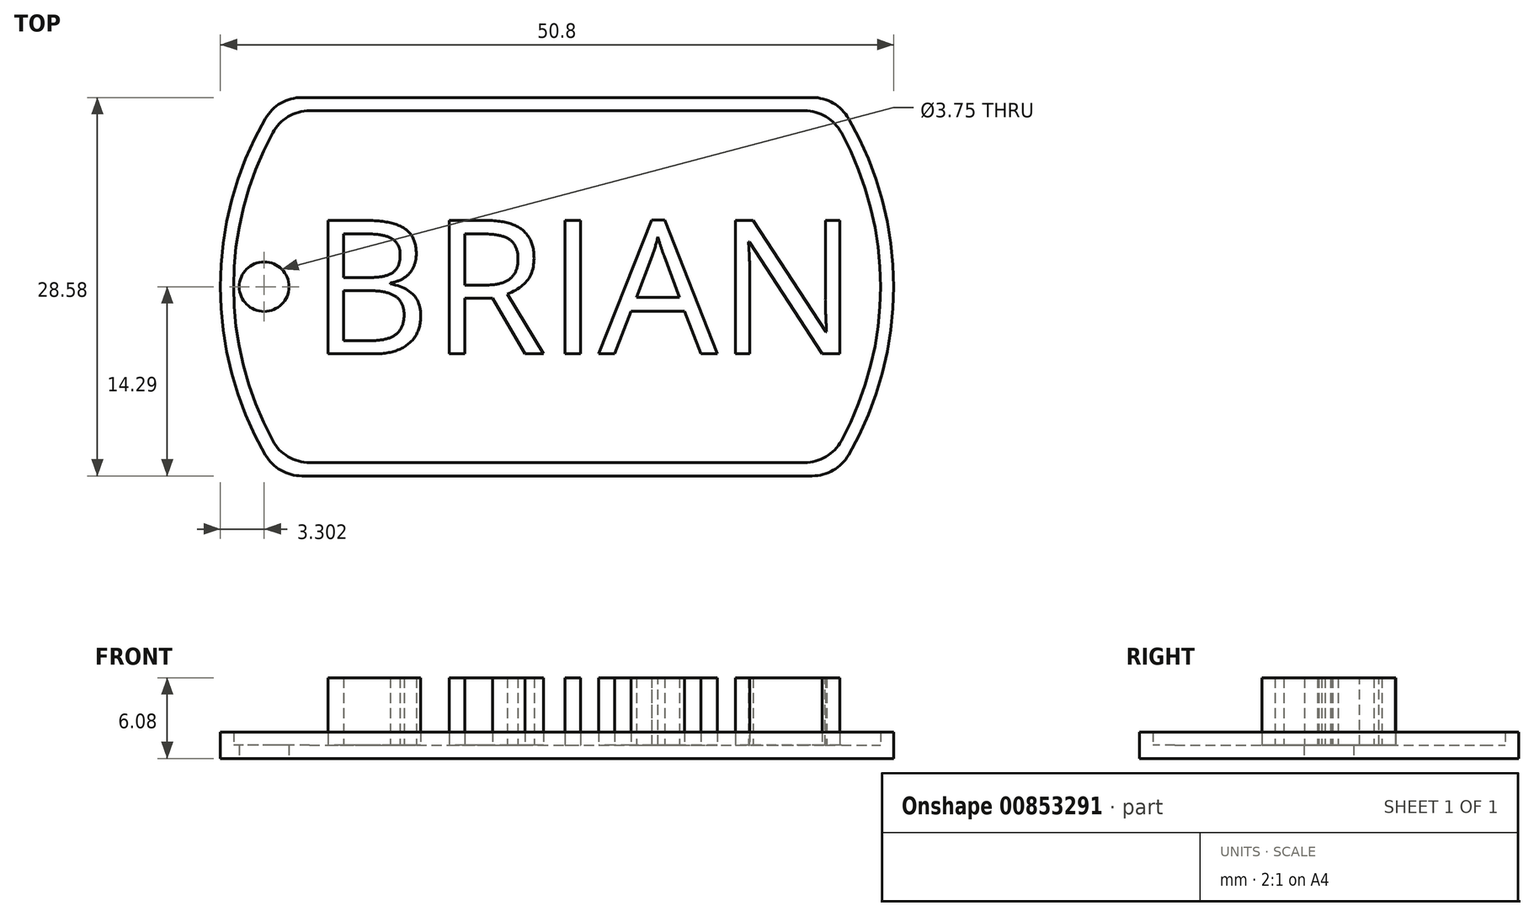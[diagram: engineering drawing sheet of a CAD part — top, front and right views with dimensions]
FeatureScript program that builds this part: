
annotation { "Feature Type Name" : "Feature", "Feature Type Description" : "" }
export const myFeature = defineFeature(function(context is Context, id is Id, definition is map)
    precondition{}
    {
        {
            var Q0;
            Q0=qCreatedBy(makeId("Top.planeOp"),FACE);
            var sketch = newSketch(context, id + "F0", { "sketchPlane" : qUnion([Q0])});
            skArc(sketch, "E0", {"start": v(-22, 12.7) * mm, "mid": v(-25.4, 0) * mm, "end": v(-22, -12.7) * mm});
            skLineSegment(sketch, "E1.top", {"start": v(-19.25, -14.29) * mm, "end": v(19.25, -14.29) * mm});
            skArc(sketch, "E2.trimOffspring", {"start": v(22, -12.7) * mm, "mid": v(25.4, 0) * mm, "end": v(22, 12.7) * mm});
            skLineSegment(sketch, "E3", {"start": v(-19.25, 14.29) * mm, "end": v(19.25, 14.29) * mm});
            skPoint(sketch, "E4.visualSharp", {"position": v(-21, 14.29) * mm});
            skArc(sketch, "E4.filletArc", {"start": v(-19.25, 14.29) * mm, "mid": v(-20.83, 13.86) * mm, "end": v(-22, 12.7) * mm});
            skPoint(sketch, "E5.visualSharp", {"position": v(21, 14.29) * mm});
            skArc(sketch, "E5.filletArc", {"start": v(22, 12.7) * mm, "mid": v(20.83, 13.86) * mm, "end": v(19.25, 14.29) * mm});
            skPoint(sketch, "E6.visualSharp", {"position": v(21, -14.29) * mm});
            skArc(sketch, "E6.filletArc", {"start": v(19.25, -14.29) * mm, "mid": v(20.83, -13.86) * mm, "end": v(22, -12.7) * mm});
            skPoint(sketch, "E7.visualSharp", {"position": v(-21, -14.29) * mm});
            skArc(sketch, "E7.filletArc", {"start": v(-22, -12.7) * mm, "mid": v(-20.83, -13.86) * mm, "end": v(-19.25, -14.29) * mm});
            skCircle(sketch, "E8", {"center": v(-22.1, 0) * mm, "radius": 1.87 * mm});
            skSolve(sketch);
        }
        {
            var Q0;
            Q0=makeQuery(id+"F0.imprint","IMPRINT",FACE,{"disambiguationData":[TD([[makeQuery(id+"F0.imprint","IMPRINT",EDGE,{"derivedFrom":sQuery(id+"F0.wireOp",EDGE,"E0")}),1.0]])]});
            extrude(context, id + "F1", {"entities" : qUnion([Q0]), "depth" : 1 * mm, "offsetDistance" : 25.4 * mm});
        }
        {
            var Q0;
            Q0=makeQuery(id+"F1.opExtrude","CAP_FACE",FACE,{"disambiguationData":[OSD([sQuery(id+"F0.wireOp",EDGE,"E0"),sQuery(id+"F0.wireOp",EDGE,"E1.top"),sQuery(id+"F0.wireOp",EDGE,"E2.trimOffspring"),sQuery(id+"F0.wireOp",EDGE,"E3"),sQuery(id+"F0.wireOp",EDGE,"E4.filletArc"),sQuery(id+"F0.wireOp",EDGE,"E5.filletArc"),sQuery(id+"F0.wireOp",EDGE,"E6.filletArc"),sQuery(id+"F0.wireOp",EDGE,"E7.filletArc")])],"isStart":false});
            var sketch = newSketch(context, id + "F2", { "sketchPlane" : qUnion([Q0])});
            skLineSegment(sketch, "E9.0", {"start": v(-18.66, 13.29) * mm, "end": v(18.66, 13.29) * mm});
            skArc(sketch, "E9.1", {"start": v(-21.45, 11.63) * mm, "mid": v(-24.4, 0) * mm, "end": v(-21.45, -11.63) * mm});
            skLineSegment(sketch, "E9.2", {"start": v(-18.66, -13.29) * mm, "end": v(18.66, -13.29) * mm});
            skArc(sketch, "E9.3", {"start": v(21.45, -11.63) * mm, "mid": v(24.4, 0) * mm, "end": v(21.45, 11.63) * mm});
            skPoint(sketch, "E10.visualSharp", {"position": v(-20.46, 13.29) * mm});
            skArc(sketch, "E10.filletArc", {"start": v(-18.66, 13.29) * mm, "mid": v(-20.29, 12.84) * mm, "end": v(-21.45, 11.63) * mm});
            skPoint(sketch, "E11.visualSharp", {"position": v(20.46, 13.29) * mm});
            skArc(sketch, "E11.filletArc", {"start": v(21.45, 11.63) * mm, "mid": v(20.29, 12.84) * mm, "end": v(18.66, 13.29) * mm});
            skPoint(sketch, "E12.visualSharp", {"position": v(20.46, -13.29) * mm});
            skArc(sketch, "E12.filletArc", {"start": v(18.66, -13.29) * mm, "mid": v(20.29, -12.84) * mm, "end": v(21.45, -11.63) * mm});
            skPoint(sketch, "E13.visualSharp", {"position": v(-20.46, -13.29) * mm});
            skArc(sketch, "E13.filletArc", {"start": v(-21.45, -11.63) * mm, "mid": v(-20.29, -12.84) * mm, "end": v(-18.66, -13.29) * mm});
            skLineSegment(sketch, "E14.0", {"start": v(-19.25, 14.29) * mm, "end": v(19.25, 14.29) * mm});
            skArc(sketch, "E14.1", {"start": v(-22, 12.7) * mm, "mid": v(-25.4, 0) * mm, "end": v(-22, -12.7) * mm});
            skLineSegment(sketch, "E14.2", {"start": v(-19.25, -14.29) * mm, "end": v(19.25, -14.29) * mm});
            skArc(sketch, "E14.3", {"start": v(22, -12.7) * mm, "mid": v(25.4, 0) * mm, "end": v(22, 12.7) * mm});
            skPoint(sketch, "E15.visualSharp", {"position": v(-21, -14.29) * mm});
            skArc(sketch, "E15.filletArc", {"start": v(-22, -12.7) * mm, "mid": v(-20.83, -13.86) * mm, "end": v(-19.25, -14.29) * mm});
            skPoint(sketch, "E16.visualSharp", {"position": v(21, -14.29) * mm});
            skArc(sketch, "E16.filletArc", {"start": v(19.25, -14.29) * mm, "mid": v(20.83, -13.86) * mm, "end": v(22, -12.7) * mm});
            skPoint(sketch, "E17.visualSharp", {"position": v(21, 14.29) * mm});
            skArc(sketch, "E17.filletArc", {"start": v(22, 12.7) * mm, "mid": v(20.83, 13.86) * mm, "end": v(19.25, 14.29) * mm});
            skPoint(sketch, "E18.visualSharp", {"position": v(-21, 14.29) * mm});
            skArc(sketch, "E18.filletArc", {"start": v(-19.25, 14.29) * mm, "mid": v(-20.83, 13.86) * mm, "end": v(-22, 12.7) * mm});
            skSolve(sketch);
        }
        {
            var Q0;
            Q0=makeQuery(id+"F2.imprint","IMPRINT",FACE,{"disambiguationData":[TD([[makeQuery(id+"F2.imprint","IMPRINT",EDGE,{"derivedFrom":sQuery(id+"F2.wireOp",EDGE,"E9.0")}),1.0]])]});
            extrude(context, id + "F3", {"entities" : qUnion([Q0]), "operationType" : NewBodyOperationType.ADD, "depth" : 1 * mm, "offsetDistance" : 25.4 * mm});
        }
        {
            var Q0;
            Q0=makeQuery(id+"F1.opExtrude","CAP_FACE",FACE,{"disambiguationData":[OSD([sQuery(id+"F0.wireOp",EDGE,"E0"),sQuery(id+"F0.wireOp",EDGE,"E1.top"),sQuery(id+"F0.wireOp",EDGE,"E2.trimOffspring"),sQuery(id+"F0.wireOp",EDGE,"E3"),sQuery(id+"F0.wireOp",EDGE,"E4.filletArc"),sQuery(id+"F0.wireOp",EDGE,"E5.filletArc"),sQuery(id+"F0.wireOp",EDGE,"E6.filletArc"),sQuery(id+"F0.wireOp",EDGE,"E7.filletArc"),sQuery(id+"F0.wireOp",EDGE,"E8")])],"isStart":false});
            var sketch = newSketch(context, id + "F4", { "sketchPlane" : qUnion([Q0])});
            skText(sketch, "E19", { "text": "BRIAN", "fontName": "OpenSans-Regular.ttf"});
            const initialGuessF4  = {"E19": [-0.01865, -0.00507, 1, 0, 0.01016]};
            skSetInitialGuess(sketch, initialGuessF4);
            skSolve(sketch);
        }
        {
            var Q0;
            Q0 = qSketchRegion(id + "F4", true);
            extrude(context, id + "F5", {"entities" : qUnion([Q0]), "operationType" : NewBodyOperationType.ADD, "depth" : 5.08 * mm, "offsetDistance" : 25.4 * mm});
        }
    });
